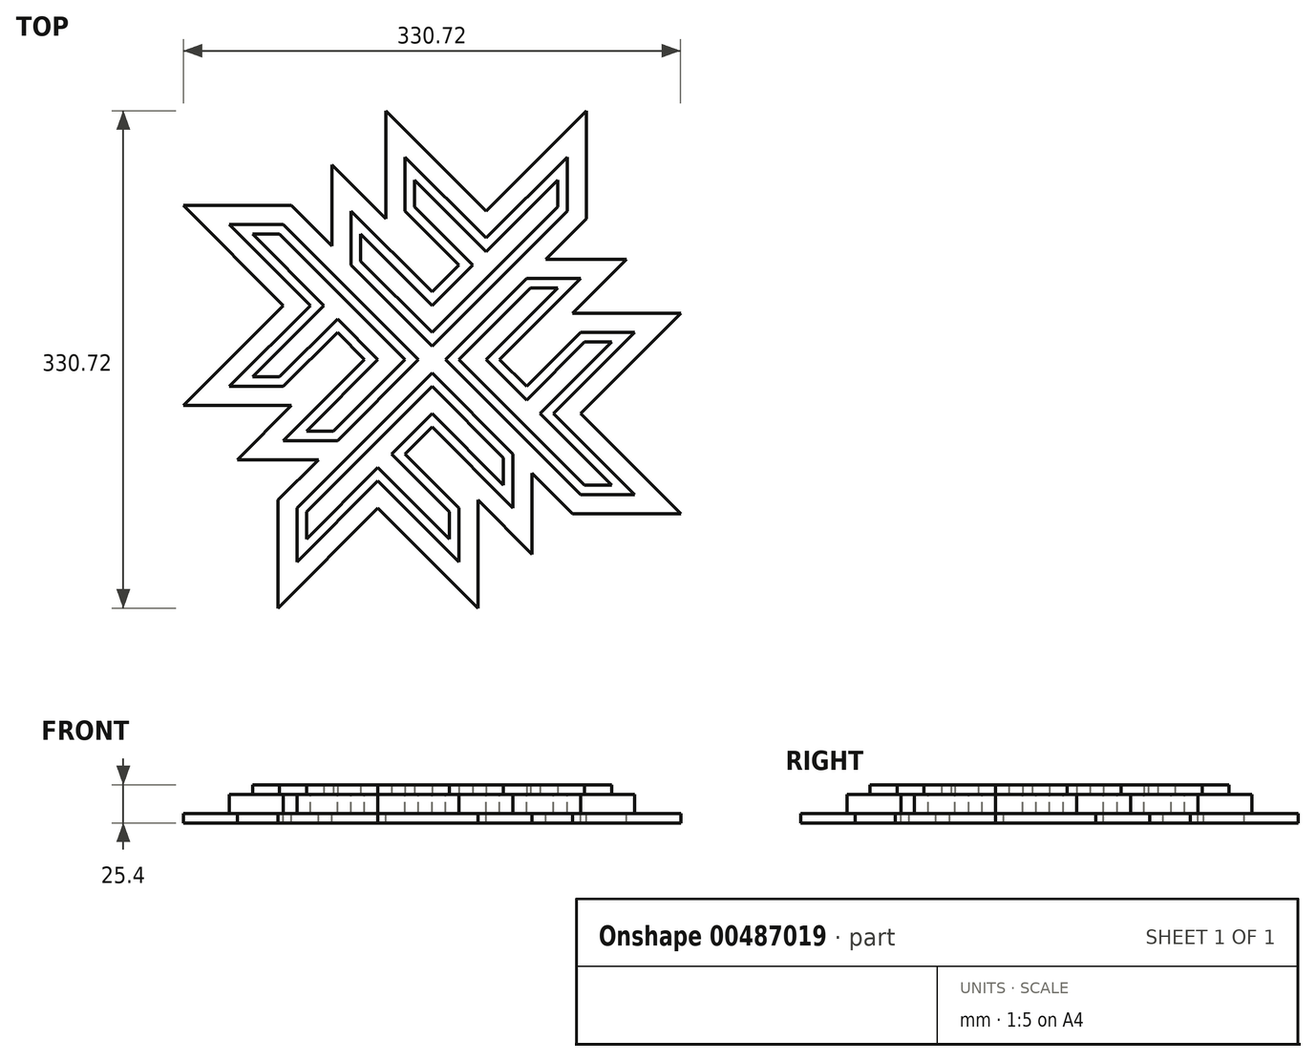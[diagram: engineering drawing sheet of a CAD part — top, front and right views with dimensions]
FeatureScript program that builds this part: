
annotation { "Feature Type Name" : "Feature", "Feature Type Description" : "" }
export const myFeature = defineFeature(function(context is Context, id is Id, definition is map)
    precondition{}
    {
        {
            var Q0;
            Q0=qCreatedBy(makeId("Top.planeOp"),FACE);
            var sketch = newSketch(context, id + "F0", { "sketchPlane" : qUnion([Q0])});
            skLineSegment(sketch, "E0", {"start": v(0, -30.17) * mm, "end": v(0, 96.83) * mm});
            skLineSegment(sketch, "E1", {"start": v(0, 96.83) * mm, "end": v(76.2, 96.83) * mm});
            skLineSegment(sketch, "E2", {"start": v(76.2, 96.83) * mm, "end": v(101.6, 71.43) * mm});
            skLineSegment(sketch, "E3", {"start": v(76.2, 96.83) * mm, "end": v(76.2, 71.43) * mm, "construction": true});
            skLineSegment(sketch, "E4", {"start": v(101.6, 71.43) * mm, "end": v(25.4, 71.43) * mm});
            skLineSegment(sketch, "E5", {"start": v(25.4, 71.43) * mm, "end": v(25.4, 46.03) * mm});
            skLineSegment(sketch, "E6", {"start": v(25.4, 46.03) * mm, "end": v(76.2, 46.03) * mm});
            skLineSegment(sketch, "E7", {"start": v(76.2, 46.03) * mm, "end": v(76.2, 20.63) * mm, "construction": true});
            skLineSegment(sketch, "E8", {"start": v(76.2, 46.03) * mm, "end": v(101.6, 20.63) * mm});
            skLineSegment(sketch, "E9", {"start": v(101.6, 20.63) * mm, "end": v(25.4, 20.63) * mm});
            skLineSegment(sketch, "E10", {"start": v(25.4, 20.63) * mm, "end": v(25.4, -55.57) * mm});
            skLineSegment(sketch, "E11", {"start": v(0, -30.17) * mm, "end": v(25.4, -55.57) * mm});
            skLineSegment(sketch, "E12.0", {"start": v(6.35, -27.54) * mm, "end": v(6.35, 90.48) * mm});
            skLineSegment(sketch, "E12.1", {"start": v(6.35, 90.48) * mm, "end": v(73.57, 90.48) * mm});
            skLineSegment(sketch, "E12.2", {"start": v(6.35, -27.54) * mm, "end": v(19.05, -40.24) * mm});
            skLineSegment(sketch, "E12.3", {"start": v(73.57, 90.48) * mm, "end": v(86.27, 77.78) * mm});
            skLineSegment(sketch, "E12.4", {"start": v(86.27, 77.78) * mm, "end": v(19.05, 77.78) * mm});
            skLineSegment(sketch, "E12.5", {"start": v(19.05, 77.78) * mm, "end": v(19.05, 39.68) * mm});
            skLineSegment(sketch, "E12.6", {"start": v(19.05, 26.98) * mm, "end": v(19.05, -40.24) * mm});
            skLineSegment(sketch, "E12.7", {"start": v(86.27, 26.98) * mm, "end": v(19.05, 26.98) * mm});
            skLineSegment(sketch, "E12.8", {"start": v(73.57, 39.68) * mm, "end": v(86.27, 26.98) * mm});
            skLineSegment(sketch, "E12.9", {"start": v(19.05, 39.68) * mm, "end": v(73.57, 39.68) * mm});
            skSolve(sketch);
        }
        {
            var Q0;
            Q0=makeQuery(id+"F0.imprint","IMPRINT",FACE,{"disambiguationData":[TD([[makeQuery(id+"F0.imprint","IMPRINT",EDGE,{"derivedFrom":sQuery(id+"F0.wireOp",EDGE,"E0")}),-1.0]])]});
            var Q1;
            Q1=makeQuery(id+"F0.imprint","IMPRINT",FACE,{"disambiguationData":[TD([[makeQuery(id+"F0.imprint","IMPRINT",EDGE,{"derivedFrom":sQuery(id+"F0.wireOp",EDGE,"E12.0")}),-1.0]])]});
            extrude(context, id + "F1", {"entities" : qUnion([Q0, Q1]), "oppositeDirection" : true, "depth" : 12.7 * mm});
        }
        {
            var Q0;
            Q0=makeQuery(id+"F1.opExtrude","CAP_FACE",FACE,{"disambiguationData":[OSD([sQuery(id+"F0.wireOp",EDGE,"E0"),sQuery(id+"F0.wireOp",EDGE,"E1"),sQuery(id+"F0.wireOp",EDGE,"E2"),sQuery(id+"F0.wireOp",EDGE,"E4"),sQuery(id+"F0.wireOp",EDGE,"E5"),sQuery(id+"F0.wireOp",EDGE,"E6"),sQuery(id+"F0.wireOp",EDGE,"E8"),sQuery(id+"F0.wireOp",EDGE,"E9"),sQuery(id+"F0.wireOp",EDGE,"E10"),sQuery(id+"F0.wireOp",EDGE,"E11")])],"isStart":true});
            var sketch = newSketch(context, id + "F2", { "sketchPlane" : qUnion([Q0])});
            skLineSegment(sketch, "E13", {"start": v(0, 96.83) * mm, "end": v(-6.35, 96.83) * mm, "construction": true});
            skLineSegment(sketch, "E14", {"start": v(-6.35, 96.83) * mm, "end": v(-6.35, 103.18) * mm, "construction": true});
            skPoint(sketch, "E15", {"position": v(-6.35, 103.18) * mm});
            skSolve(sketch);
        }
        {
            var Q0;
            Q0=qCreatedBy(makeId("Right.planeOp"),FACE);
            cPlane(context, id + "F3", {"entities" : qUnion([Q0]), "cplaneType" : CPlaneType.OFFSET, "offset" : 6.35 * mm, "oppositeDirection" : true, "width" : 152.4 * mm, "height" : 152.4 * mm});
        }
        {
            var Q0;
            Q0=qCreatedBy(id+"F3.planeOp",FACE);
            var sketch = newSketch(context, id + "F4", { "sketchPlane" : qUnion([Q0])});
            skPoint(sketch, "E16.0", {"position": v(103.18, 0) * mm});
            skLineSegment(sketch, "E17", {"start": v(103.18, 0) * mm, "end": v(103.18, -12.7) * mm, "construction": true});
            skSolve(sketch);
        }
        {
            var Q0;
            Q0=makeQuery(id+"F1.opExtrude","SWEPT_BODY",BODY,{"disambiguationData":[OSD([sQuery(id+"F0.wireOp",EDGE,"E0"),sQuery(id+"F0.wireOp",EDGE,"E1"),sQuery(id+"F0.wireOp",EDGE,"E2"),sQuery(id+"F0.wireOp",EDGE,"E4"),sQuery(id+"F0.wireOp",EDGE,"E5"),sQuery(id+"F0.wireOp",EDGE,"E6"),sQuery(id+"F0.wireOp",EDGE,"E8"),sQuery(id+"F0.wireOp",EDGE,"E9"),sQuery(id+"F0.wireOp",EDGE,"E10"),sQuery(id+"F0.wireOp",EDGE,"E11")])]});
            var Q1;
            Q1=sQuery(id+"F4.wireOp",EDGE,"E17");
            circularPattern(context, id + "F5", {"entities" : qUnion([Q0]), "axis" : qUnion([Q1]), "angle" : 360 * degree, "instanceCount" : 4, "equalSpace" : true});
        }
        {
            var Q0;
            Q0=makeQuery(id+"F5.opPattern","COPY",FACE,{"derivedFrom":makeQuery(id+"F1.opExtrude","CAP_FACE",FACE,{"disambiguationData":[OSD([sQuery(id+"F0.wireOp",EDGE,"E0"),sQuery(id+"F0.wireOp",EDGE,"E1"),sQuery(id+"F0.wireOp",EDGE,"E2"),sQuery(id+"F0.wireOp",EDGE,"E4"),sQuery(id+"F0.wireOp",EDGE,"E5"),sQuery(id+"F0.wireOp",EDGE,"E6"),sQuery(id+"F0.wireOp",EDGE,"E8"),sQuery(id+"F0.wireOp",EDGE,"E9"),sQuery(id+"F0.wireOp",EDGE,"E10"),sQuery(id+"F0.wireOp",EDGE,"E11")])],"isStart":false}),"instanceName":"1"});
            var sketch = newSketch(context, id + "F6", { "sketchPlane" : qUnion([Q0])});
            skLineSegment(sketch, "E18.0", {"start": v(0, -185.73) * mm, "end": v(25.4, -211.13) * mm});
            skLineSegment(sketch, "E18.1", {"start": v(-12.7, -236.53) * mm, "end": v(-12.7, -109.53) * mm});
            skLineSegment(sketch, "E18.2", {"start": v(-12.7, -236.53) * mm, "end": v(-38.1, -261.93) * mm});
            skLineSegment(sketch, "E18.3", {"start": v(-38.1, -185.73) * mm, "end": v(-38.1, -261.93) * mm});
            skLineSegment(sketch, "E18.4", {"start": v(-114.3, -185.73) * mm, "end": v(-38.1, -185.73) * mm});
            skLineSegment(sketch, "E18.5", {"start": v(-88.9, -160.33) * mm, "end": v(-114.3, -185.73) * mm});
            skLineSegment(sketch, "E18.6", {"start": v(-38.1, -160.33) * mm, "end": v(-88.9, -160.33) * mm});
            skLineSegment(sketch, "E18.7", {"start": v(-38.1, -134.93) * mm, "end": v(-38.1, -160.33) * mm});
            skLineSegment(sketch, "E18.8", {"start": v(-114.3, -134.93) * mm, "end": v(-38.1, -134.93) * mm});
            skLineSegment(sketch, "E18.9", {"start": v(-88.9, -109.53) * mm, "end": v(-114.3, -134.93) * mm});
            skLineSegment(sketch, "E18.10", {"start": v(-12.7, -109.53) * mm, "end": v(-88.9, -109.53) * mm});
            skLineSegment(sketch, "E18.11", {"start": v(-139.7, -96.83) * mm, "end": v(-12.7, -96.83) * mm});
            skLineSegment(sketch, "E18.12", {"start": v(-139.7, -96.83) * mm, "end": v(-165.1, -71.43) * mm});
            skLineSegment(sketch, "E18.13", {"start": v(-88.9, -71.43) * mm, "end": v(-165.1, -71.43) * mm});
            skLineSegment(sketch, "E18.14", {"start": v(-88.9, 4.77) * mm, "end": v(-88.9, -71.43) * mm});
            skLineSegment(sketch, "E18.15", {"start": v(-63.5, -20.63) * mm, "end": v(-88.9, 4.77) * mm});
            skLineSegment(sketch, "E18.16", {"start": v(-63.5, -71.43) * mm, "end": v(-63.5, -20.63) * mm});
            skLineSegment(sketch, "E18.17", {"start": v(-38.1, -71.43) * mm, "end": v(-63.5, -71.43) * mm});
            skLineSegment(sketch, "E18.18", {"start": v(-38.1, 4.77) * mm, "end": v(-38.1, -71.43) * mm});
            skLineSegment(sketch, "E18.19", {"start": v(-12.7, -20.63) * mm, "end": v(-38.1, 4.77) * mm});
            skLineSegment(sketch, "E18.20", {"start": v(-12.7, -96.83) * mm, "end": v(-12.7, -20.63) * mm});
            skLineSegment(sketch, "E18.21", {"start": v(0, 30.17) * mm, "end": v(0, -96.83) * mm});
            skLineSegment(sketch, "E18.22", {"start": v(0, -96.83) * mm, "end": v(76.2, -96.83) * mm});
            skLineSegment(sketch, "E18.23", {"start": v(76.2, -96.83) * mm, "end": v(101.6, -71.43) * mm});
            skLineSegment(sketch, "E18.24", {"start": v(101.6, -71.43) * mm, "end": v(25.4, -71.43) * mm});
            skLineSegment(sketch, "E18.25", {"start": v(25.4, -71.43) * mm, "end": v(25.4, -46.03) * mm});
            skLineSegment(sketch, "E18.26", {"start": v(25.4, -46.03) * mm, "end": v(76.2, -46.03) * mm});
            skLineSegment(sketch, "E18.27", {"start": v(76.2, -46.03) * mm, "end": v(101.6, -20.63) * mm});
            skLineSegment(sketch, "E18.28", {"start": v(101.6, -20.63) * mm, "end": v(25.4, -20.63) * mm});
            skLineSegment(sketch, "E18.29", {"start": v(25.4, -20.63) * mm, "end": v(25.4, 55.57) * mm});
            skLineSegment(sketch, "E18.30", {"start": v(0, 30.17) * mm, "end": v(25.4, 55.57) * mm});
            skLineSegment(sketch, "E18.31", {"start": v(127, -109.53) * mm, "end": v(0, -109.53) * mm});
            skLineSegment(sketch, "E18.32", {"start": v(0, -109.53) * mm, "end": v(0, -185.73) * mm});
            skLineSegment(sketch, "E18.33", {"start": v(25.4, -211.13) * mm, "end": v(25.4, -134.93) * mm});
            skLineSegment(sketch, "E18.34", {"start": v(25.4, -134.93) * mm, "end": v(50.8, -134.93) * mm});
            skLineSegment(sketch, "E18.35", {"start": v(50.8, -134.93) * mm, "end": v(50.8, -185.73) * mm});
            skLineSegment(sketch, "E18.36", {"start": v(50.8, -185.73) * mm, "end": v(76.2, -211.13) * mm});
            skLineSegment(sketch, "E18.37", {"start": v(76.2, -211.13) * mm, "end": v(76.2, -134.93) * mm});
            skLineSegment(sketch, "E18.38", {"start": v(76.2, -134.93) * mm, "end": v(152.4, -134.93) * mm});
            skLineSegment(sketch, "E18.39", {"start": v(127, -109.53) * mm, "end": v(152.4, -134.93) * mm});
            skLineSegment(sketch, "E19.0", {"start": v(0, -241.79) * mm, "end": v(-50.8, -292.59) * mm});
            skLineSegment(sketch, "E19.1", {"start": v(-50.8, -198.43) * mm, "end": v(-50.8, -292.59) * mm});
            skLineSegment(sketch, "E19.3", {"start": v(-144.96, -198.43) * mm, "end": v(-50.8, -198.43) * mm});
            skLineSegment(sketch, "E19.4", {"start": v(-94.16, -147.63) * mm, "end": v(-144.96, -198.43) * mm});
            skLineSegment(sketch, "E20", {"start": v(-144.96, -147.63) * mm, "end": v(-94.16, -147.63) * mm});
            skPoint(sketch, "E21.0", {"position": v(-6.35, -103.18) * mm});
            skLineSegment(sketch, "E22.1.1", {"start": v(132.26, -96.83) * mm, "end": v(183.06, -147.63) * mm});
            skLineSegment(sketch, "E22.1.2", {"start": v(88.9, -147.63) * mm, "end": v(183.06, -147.63) * mm});
            skLineSegment(sketch, "E22.1.3", {"start": v(88.9, -241.79) * mm, "end": v(88.9, -147.63) * mm});
            skLineSegment(sketch, "E22.1.4", {"start": v(38.1, -190.99) * mm, "end": v(88.9, -241.79) * mm});
            skLineSegment(sketch, "E22.1.5", {"start": v(38.1, -241.79) * mm, "end": v(38.1, -190.99) * mm});
            skLineSegment(sketch, "E22.2.1", {"start": v(-12.7, 35.43) * mm, "end": v(38.1, 86.23) * mm});
            skLineSegment(sketch, "E22.2.2", {"start": v(38.1, -7.93) * mm, "end": v(38.1, 86.23) * mm});
            skLineSegment(sketch, "E22.2.3", {"start": v(132.26, -7.93) * mm, "end": v(38.1, -7.93) * mm});
            skLineSegment(sketch, "E22.2.4", {"start": v(81.46, -58.73) * mm, "end": v(132.26, -7.93) * mm});
            skLineSegment(sketch, "E22.2.5", {"start": v(132.26, -58.73) * mm, "end": v(81.46, -58.73) * mm});
            skLineSegment(sketch, "E22.3.1", {"start": v(-144.96, -109.53) * mm, "end": v(-195.76, -58.73) * mm});
            skLineSegment(sketch, "E22.3.2", {"start": v(-101.6, -58.73) * mm, "end": v(-195.76, -58.73) * mm});
            skLineSegment(sketch, "E22.3.3", {"start": v(-101.6, 35.43) * mm, "end": v(-101.6, -58.73) * mm});
            skLineSegment(sketch, "E22.3.4", {"start": v(-50.8, -15.37) * mm, "end": v(-101.6, 35.43) * mm});
            skLineSegment(sketch, "E22.3.5", {"start": v(-50.8, 35.43) * mm, "end": v(-50.8, -15.37) * mm});
            skLineSegment(sketch, "E23", {"start": v(0, -241.79) * mm, "end": v(0, -203.69) * mm});
            skLineSegment(sketch, "E24", {"start": v(38.1, -241.79) * mm, "end": v(0, -203.69) * mm});
            skLineSegment(sketch, "E25", {"start": v(132.26, -96.83) * mm, "end": v(94.16, -96.83) * mm});
            skLineSegment(sketch, "E26", {"start": v(132.26, -58.73) * mm, "end": v(94.16, -96.83) * mm});
            skLineSegment(sketch, "E27", {"start": v(-12.7, 35.43) * mm, "end": v(-12.7, -2.67) * mm});
            skLineSegment(sketch, "E28", {"start": v(-12.7, -2.67) * mm, "end": v(-50.8, 35.43) * mm});
            skLineSegment(sketch, "E29", {"start": v(-144.96, -109.53) * mm, "end": v(-106.86, -109.53) * mm});
            skLineSegment(sketch, "E30", {"start": v(-144.96, -147.63) * mm, "end": v(-106.86, -109.53) * mm});
            skSolve(sketch);
        }
        {
            var Q0;
            Q0=makeQuery(id+"F6.imprint","IMPRINT",FACE,{"disambiguationData":[TD([[makeQuery(id+"F6.imprint","IMPRINT",EDGE,{"derivedFrom":sQuery(id+"F6.wireOp",EDGE,"E18.0")}),-1.0]])]});
            var Q1;
            Q1=makeQuery(id+"F6.imprint","IMPRINT",FACE,{"disambiguationData":[TD([[makeQuery(id+"F6.imprint","IMPRINT",EDGE,{"derivedFrom":sQuery(id+"F6.wireOp",EDGE,"E18.11")}),1.0]])]});
            var Q2;
            Q2=makeQuery(id+"F6.imprint","IMPRINT",FACE,{"disambiguationData":[TD([[makeQuery(id+"F6.imprint","IMPRINT",EDGE,{"derivedFrom":sQuery(id+"F6.wireOp",EDGE,"E18.21")}),1.0]])]});
            var Q3;
            Q3=makeQuery(id+"F6.imprint","IMPRINT",FACE,{"disambiguationData":[TD([[makeQuery(id+"F6.imprint","IMPRINT",EDGE,{"derivedFrom":sQuery(id+"F6.wireOp",EDGE,"E18.0")}),1.0]])]});
            var Q4;
            Q4=makeQuery(id+"F6.imprint","IMPRINT",FACE,{"disambiguationData":[TD([[makeQuery(id+"F6.imprint","IMPRINT",EDGE,{"derivedFrom":sQuery(id+"F6.wireOp",EDGE,"E18.1")}),1.0]])]});
            extrude(context, id + "F7", {"entities" : qUnion([Q0, Q1, Q2, Q3, Q4]), "depth" : 6.35 * mm});
        }
        {
            var Q0;
            Q0=makeQuery(id+"F7.opExtrude","SWEPT_BODY",BODY,{"disambiguationData":[OSD([sQuery(id+"F6.wireOp",EDGE,"E19.0"),sQuery(id+"F6.wireOp",EDGE,"E19.1"),sQuery(id+"F6.wireOp",EDGE,"E19.3"),sQuery(id+"F6.wireOp",EDGE,"E19.4"),sQuery(id+"F6.wireOp",EDGE,"E20"),sQuery(id+"F6.wireOp",EDGE,"E22.1.1"),sQuery(id+"F6.wireOp",EDGE,"E22.1.2"),sQuery(id+"F6.wireOp",EDGE,"E22.1.3"),sQuery(id+"F6.wireOp",EDGE,"E22.1.4"),sQuery(id+"F6.wireOp",EDGE,"E22.1.5"),sQuery(id+"F6.wireOp",EDGE,"E22.2.1"),sQuery(id+"F6.wireOp",EDGE,"E22.2.2"),sQuery(id+"F6.wireOp",EDGE,"E22.2.3"),sQuery(id+"F6.wireOp",EDGE,"E22.2.4"),sQuery(id+"F6.wireOp",EDGE,"E22.2.5"),sQuery(id+"F6.wireOp",EDGE,"E22.3.1"),sQuery(id+"F6.wireOp",EDGE,"E22.3.2"),sQuery(id+"F6.wireOp",EDGE,"E22.3.3"),sQuery(id+"F6.wireOp",EDGE,"E22.3.4"),sQuery(id+"F6.wireOp",EDGE,"E22.3.5"),sQuery(id+"F6.wireOp",EDGE,"E23"),sQuery(id+"F6.wireOp",EDGE,"E24"),sQuery(id+"F6.wireOp",EDGE,"E25"),sQuery(id+"F6.wireOp",EDGE,"E26"),sQuery(id+"F6.wireOp",EDGE,"E27"),sQuery(id+"F6.wireOp",EDGE,"E28"),sQuery(id+"F6.wireOp",EDGE,"E29"),sQuery(id+"F6.wireOp",EDGE,"E30")])]});
            var Q1;
            Q1=makeQuery(id+"F1.opExtrude","SWEPT_BODY",BODY,{"disambiguationData":[OSD([sQuery(id+"F0.wireOp",EDGE,"E0"),sQuery(id+"F0.wireOp",EDGE,"E1"),sQuery(id+"F0.wireOp",EDGE,"E2"),sQuery(id+"F0.wireOp",EDGE,"E4"),sQuery(id+"F0.wireOp",EDGE,"E5"),sQuery(id+"F0.wireOp",EDGE,"E6"),sQuery(id+"F0.wireOp",EDGE,"E8"),sQuery(id+"F0.wireOp",EDGE,"E9"),sQuery(id+"F0.wireOp",EDGE,"E10"),sQuery(id+"F0.wireOp",EDGE,"E11")])]});
            var Q2;
            Q2=makeQuery(id+"F5.opPattern","COPY",BODY,{"derivedFrom":makeQuery(id+"F1.opExtrude","SWEPT_BODY",BODY,{"disambiguationData":[OSD([sQuery(id+"F0.wireOp",EDGE,"E0"),sQuery(id+"F0.wireOp",EDGE,"E1"),sQuery(id+"F0.wireOp",EDGE,"E2"),sQuery(id+"F0.wireOp",EDGE,"E4"),sQuery(id+"F0.wireOp",EDGE,"E5"),sQuery(id+"F0.wireOp",EDGE,"E6"),sQuery(id+"F0.wireOp",EDGE,"E8"),sQuery(id+"F0.wireOp",EDGE,"E9"),sQuery(id+"F0.wireOp",EDGE,"E10"),sQuery(id+"F0.wireOp",EDGE,"E11")])]}),"instanceName":"1"});
            var Q3;
            Q3=makeQuery(id+"F5.opPattern","COPY",BODY,{"derivedFrom":makeQuery(id+"F1.opExtrude","SWEPT_BODY",BODY,{"disambiguationData":[OSD([sQuery(id+"F0.wireOp",EDGE,"E0"),sQuery(id+"F0.wireOp",EDGE,"E1"),sQuery(id+"F0.wireOp",EDGE,"E2"),sQuery(id+"F0.wireOp",EDGE,"E4"),sQuery(id+"F0.wireOp",EDGE,"E5"),sQuery(id+"F0.wireOp",EDGE,"E6"),sQuery(id+"F0.wireOp",EDGE,"E8"),sQuery(id+"F0.wireOp",EDGE,"E9"),sQuery(id+"F0.wireOp",EDGE,"E10"),sQuery(id+"F0.wireOp",EDGE,"E11")])]}),"instanceName":"2"});
            var Q4;
            Q4=makeQuery(id+"F5.opPattern","COPY",BODY,{"derivedFrom":makeQuery(id+"F1.opExtrude","SWEPT_BODY",BODY,{"disambiguationData":[OSD([sQuery(id+"F0.wireOp",EDGE,"E0"),sQuery(id+"F0.wireOp",EDGE,"E1"),sQuery(id+"F0.wireOp",EDGE,"E2"),sQuery(id+"F0.wireOp",EDGE,"E4"),sQuery(id+"F0.wireOp",EDGE,"E5"),sQuery(id+"F0.wireOp",EDGE,"E6"),sQuery(id+"F0.wireOp",EDGE,"E8"),sQuery(id+"F0.wireOp",EDGE,"E9"),sQuery(id+"F0.wireOp",EDGE,"E10"),sQuery(id+"F0.wireOp",EDGE,"E11")])]}),"instanceName":"3"});
            var Q5;
            Q5=sQuery(id+"F2.wireOp",VERTEX,"E15");
            var Q6;
            Q6=qCreatedBy(makeId("Origin.pointOp"),VERTEX);
            transform(context, id + "F8", {"entities" : qUnion([Q0, Q1, Q2, Q3, Q4]), "transformType" : TransformType.TRANSLATION_ENTITY, "oppositeDirectionEntity" : false, "transformLine" : qUnion([Q5, Q6]), "makeCopy" : false});
        }
        {
            var Q0;
            Q0=makeQuery(id+"F1.opExtrude","CAP_FACE",FACE,{"disambiguationData":[OSD([sQuery(id+"F0.wireOp",EDGE,"E0"),sQuery(id+"F0.wireOp",EDGE,"E1"),sQuery(id+"F0.wireOp",EDGE,"E2"),sQuery(id+"F0.wireOp",EDGE,"E4"),sQuery(id+"F0.wireOp",EDGE,"E5"),sQuery(id+"F0.wireOp",EDGE,"E6"),sQuery(id+"F0.wireOp",EDGE,"E8"),sQuery(id+"F0.wireOp",EDGE,"E9"),sQuery(id+"F0.wireOp",EDGE,"E10"),sQuery(id+"F0.wireOp",EDGE,"E11")])],"isStart":true});
            var sketch = newSketch(context, id + "F9", { "sketchPlane" : qUnion([Q0])});
            skLineSegment(sketch, "E31.0.0", {"start": v(-6.35, -6.35) * mm, "end": v(-133.35, -6.35) * mm});
            skLineSegment(sketch, "E31.0.1", {"start": v(-133.35, -6.35) * mm, "end": v(-158.75, -31.75) * mm});
            skLineSegment(sketch, "E31.0.2", {"start": v(-158.75, -31.75) * mm, "end": v(-82.55, -31.75) * mm});
            skLineSegment(sketch, "E31.0.3", {"start": v(-82.55, -31.75) * mm, "end": v(-82.55, -107.95) * mm});
            skLineSegment(sketch, "E31.0.4", {"start": v(-82.55, -107.95) * mm, "end": v(-57.15, -82.55) * mm});
            skLineSegment(sketch, "E31.0.5", {"start": v(-57.15, -82.55) * mm, "end": v(-57.15, -31.75) * mm});
            skLineSegment(sketch, "E31.0.6", {"start": v(-57.15, -31.75) * mm, "end": v(-31.75, -31.75) * mm});
            skLineSegment(sketch, "E31.0.7", {"start": v(-31.75, -31.75) * mm, "end": v(-31.75, -107.95) * mm});
            skLineSegment(sketch, "E31.0.8", {"start": v(-31.75, -107.95) * mm, "end": v(-6.35, -82.55) * mm});
            skLineSegment(sketch, "E31.0.9", {"start": v(-6.35, -82.55) * mm, "end": v(-6.35, -6.35) * mm});
            skLineSegment(sketch, "E31.2.0", {"start": v(6.35, 6.35) * mm, "end": v(133.35, 6.35) * mm});
            skLineSegment(sketch, "E31.2.1", {"start": v(133.35, 6.35) * mm, "end": v(158.75, 31.75) * mm});
            skLineSegment(sketch, "E31.2.2", {"start": v(158.75, 31.75) * mm, "end": v(82.55, 31.75) * mm});
            skLineSegment(sketch, "E31.2.3", {"start": v(82.55, 31.75) * mm, "end": v(82.55, 107.95) * mm});
            skLineSegment(sketch, "E31.2.4", {"start": v(82.55, 107.95) * mm, "end": v(57.15, 82.55) * mm});
            skLineSegment(sketch, "E31.2.5", {"start": v(57.15, 82.55) * mm, "end": v(57.15, 31.75) * mm});
            skLineSegment(sketch, "E31.2.6", {"start": v(57.15, 31.75) * mm, "end": v(31.75, 31.75) * mm});
            skLineSegment(sketch, "E31.2.7", {"start": v(31.75, 31.75) * mm, "end": v(31.75, 107.95) * mm});
            skLineSegment(sketch, "E31.2.8", {"start": v(31.75, 107.95) * mm, "end": v(6.35, 82.55) * mm});
            skLineSegment(sketch, "E31.2.9", {"start": v(6.35, 82.55) * mm, "end": v(6.35, 6.35) * mm});
            skLineSegment(sketch, "E31.3.0", {"start": v(-6.35, 6.35) * mm, "end": v(-6.35, 133.35) * mm});
            skLineSegment(sketch, "E31.3.1", {"start": v(-6.35, 133.35) * mm, "end": v(-31.75, 158.75) * mm});
            skLineSegment(sketch, "E31.3.2", {"start": v(-31.75, 158.75) * mm, "end": v(-31.75, 82.55) * mm});
            skLineSegment(sketch, "E31.3.3", {"start": v(-31.75, 82.55) * mm, "end": v(-107.95, 82.55) * mm});
            skLineSegment(sketch, "E31.3.4", {"start": v(-107.95, 82.55) * mm, "end": v(-82.55, 57.15) * mm});
            skLineSegment(sketch, "E31.3.5", {"start": v(-82.55, 57.15) * mm, "end": v(-31.75, 57.15) * mm});
            skLineSegment(sketch, "E31.3.6", {"start": v(-31.75, 57.15) * mm, "end": v(-31.75, 31.75) * mm});
            skLineSegment(sketch, "E31.3.7", {"start": v(-31.75, 31.75) * mm, "end": v(-107.95, 31.75) * mm});
            skLineSegment(sketch, "E31.3.8", {"start": v(-107.95, 31.75) * mm, "end": v(-82.55, 6.35) * mm});
            skLineSegment(sketch, "E31.3.9", {"start": v(-82.55, 6.35) * mm, "end": v(-6.35, 6.35) * mm});
            skLineSegment(sketch, "E32.0", {"start": v(6.35, -133.35) * mm, "end": v(6.35, -6.35) * mm});
            skLineSegment(sketch, "E32.1", {"start": v(6.35, -6.35) * mm, "end": v(82.55, -6.35) * mm});
            skLineSegment(sketch, "E32.2", {"start": v(82.55, -6.35) * mm, "end": v(107.95, -31.75) * mm});
            skLineSegment(sketch, "E32.3", {"start": v(107.95, -31.75) * mm, "end": v(31.75, -31.75) * mm});
            skLineSegment(sketch, "E32.4", {"start": v(31.75, -31.75) * mm, "end": v(31.75, -57.15) * mm});
            skLineSegment(sketch, "E32.5", {"start": v(31.75, -57.15) * mm, "end": v(82.55, -57.15) * mm});
            skLineSegment(sketch, "E32.6", {"start": v(82.55, -57.15) * mm, "end": v(107.95, -82.55) * mm});
            skLineSegment(sketch, "E32.7", {"start": v(107.95, -82.55) * mm, "end": v(31.75, -82.55) * mm});
            skLineSegment(sketch, "E32.8", {"start": v(31.75, -82.55) * mm, "end": v(31.75, -158.75) * mm});
            skLineSegment(sketch, "E32.9", {"start": v(6.35, -133.35) * mm, "end": v(31.75, -158.75) * mm});
            skLineSegment(sketch, "E33.0", {"start": v(12.7, -130.72) * mm, "end": v(12.7, -12.7) * mm});
            skLineSegment(sketch, "E33.1", {"start": v(12.7, -130.72) * mm, "end": v(25.4, -143.42) * mm});
            skLineSegment(sketch, "E33.2", {"start": v(12.7, -12.7) * mm, "end": v(79.92, -12.7) * mm});
            skLineSegment(sketch, "E33.3", {"start": v(25.4, -76.2) * mm, "end": v(25.4, -143.42) * mm});
            skLineSegment(sketch, "E33.4", {"start": v(92.62, -76.2) * mm, "end": v(25.4, -76.2) * mm});
            skLineSegment(sketch, "E33.5", {"start": v(79.92, -63.5) * mm, "end": v(92.62, -76.2) * mm});
            skLineSegment(sketch, "E33.6", {"start": v(79.92, -12.7) * mm, "end": v(92.62, -25.4) * mm});
            skLineSegment(sketch, "E33.7", {"start": v(92.62, -25.4) * mm, "end": v(25.4, -25.4) * mm});
            skLineSegment(sketch, "E33.8", {"start": v(25.4, -25.4) * mm, "end": v(25.4, -63.5) * mm});
            skLineSegment(sketch, "E33.9", {"start": v(25.4, -63.5) * mm, "end": v(79.92, -63.5) * mm});
            skLineSegment(sketch, "E34.0", {"start": v(-25.4, -92.62) * mm, "end": v(-12.7, -79.92) * mm});
            skLineSegment(sketch, "E34.1", {"start": v(-25.4, -25.4) * mm, "end": v(-25.4, -92.62) * mm});
            skLineSegment(sketch, "E34.2", {"start": v(-12.7, -79.92) * mm, "end": v(-12.7, -12.7) * mm});
            skLineSegment(sketch, "E34.3", {"start": v(-63.5, -25.4) * mm, "end": v(-25.4, -25.4) * mm});
            skLineSegment(sketch, "E34.4", {"start": v(-63.5, -79.92) * mm, "end": v(-63.5, -25.4) * mm});
            skLineSegment(sketch, "E34.5", {"start": v(-76.2, -92.62) * mm, "end": v(-63.5, -79.92) * mm});
            skLineSegment(sketch, "E34.6", {"start": v(-12.7, -12.7) * mm, "end": v(-130.72, -12.7) * mm});
            skLineSegment(sketch, "E34.7", {"start": v(-130.72, -12.7) * mm, "end": v(-143.42, -25.4) * mm});
            skLineSegment(sketch, "E34.8", {"start": v(-143.42, -25.4) * mm, "end": v(-76.2, -25.4) * mm});
            skLineSegment(sketch, "E34.9", {"start": v(-76.2, -25.4) * mm, "end": v(-76.2, -92.62) * mm});
            skLineSegment(sketch, "E35.0", {"start": v(-12.7, 130.72) * mm, "end": v(-25.4, 143.42) * mm});
            skLineSegment(sketch, "E35.1", {"start": v(-12.7, 12.7) * mm, "end": v(-12.7, 130.72) * mm});
            skLineSegment(sketch, "E35.2", {"start": v(-25.4, 143.42) * mm, "end": v(-25.4, 76.2) * mm});
            skLineSegment(sketch, "E35.3", {"start": v(-79.92, 12.7) * mm, "end": v(-12.7, 12.7) * mm});
            skLineSegment(sketch, "E35.4", {"start": v(-92.62, 25.4) * mm, "end": v(-79.92, 12.7) * mm});
            skLineSegment(sketch, "E35.5", {"start": v(-25.4, 25.4) * mm, "end": v(-92.62, 25.4) * mm});
            skLineSegment(sketch, "E35.6", {"start": v(-25.4, 76.2) * mm, "end": v(-92.62, 76.2) * mm});
            skLineSegment(sketch, "E35.7", {"start": v(-92.62, 76.2) * mm, "end": v(-79.92, 63.5) * mm});
            skLineSegment(sketch, "E35.8", {"start": v(-79.92, 63.5) * mm, "end": v(-25.4, 63.5) * mm});
            skLineSegment(sketch, "E35.9", {"start": v(-25.4, 63.5) * mm, "end": v(-25.4, 25.4) * mm});
            skLineSegment(sketch, "E36.0", {"start": v(63.5, 25.4) * mm, "end": v(25.4, 25.4) * mm});
            skLineSegment(sketch, "E36.1", {"start": v(63.5, 79.92) * mm, "end": v(63.5, 25.4) * mm});
            skLineSegment(sketch, "E36.2", {"start": v(25.4, 25.4) * mm, "end": v(25.4, 92.62) * mm});
            skLineSegment(sketch, "E36.3", {"start": v(76.2, 92.62) * mm, "end": v(63.5, 79.92) * mm});
            skLineSegment(sketch, "E36.4", {"start": v(76.2, 25.4) * mm, "end": v(76.2, 92.62) * mm});
            skLineSegment(sketch, "E36.5", {"start": v(143.42, 25.4) * mm, "end": v(76.2, 25.4) * mm});
            skLineSegment(sketch, "E36.6", {"start": v(25.4, 92.62) * mm, "end": v(12.7, 79.92) * mm});
            skLineSegment(sketch, "E36.7", {"start": v(12.7, 79.92) * mm, "end": v(12.7, 12.7) * mm});
            skLineSegment(sketch, "E36.8", {"start": v(12.7, 12.7) * mm, "end": v(130.72, 12.7) * mm});
            skLineSegment(sketch, "E36.9", {"start": v(130.72, 12.7) * mm, "end": v(143.42, 25.4) * mm});
            skSolve(sketch);
        }
        {
            var Q0;
            Q0=makeQuery(id+"F9.imprint","IMPRINT",FACE,{"disambiguationData":[TD([[makeQuery(id+"F9.imprint","IMPRINT",EDGE,{"derivedFrom":sQuery(id+"F9.wireOp",EDGE,"E35.0")}),1.0]])]});
            var Q1;
            Q1=makeQuery(id+"F9.imprint","IMPRINT",FACE,{"disambiguationData":[TD([[makeQuery(id+"F9.imprint","IMPRINT",EDGE,{"derivedFrom":sQuery(id+"F9.wireOp",EDGE,"E36.0")}),1.0]])]});
            var Q2;
            Q2=makeQuery(id+"F9.imprint","IMPRINT",FACE,{"disambiguationData":[TD([[makeQuery(id+"F9.imprint","IMPRINT",EDGE,{"derivedFrom":sQuery(id+"F9.wireOp",EDGE,"E33.0")}),-1.0]])]});
            var Q3;
            Q3=makeQuery(id+"F9.imprint","IMPRINT",FACE,{"disambiguationData":[TD([[makeQuery(id+"F9.imprint","IMPRINT",EDGE,{"derivedFrom":sQuery(id+"F9.wireOp",EDGE,"E34.0")}),1.0]])]});
            extrude(context, id + "F10", {"entities" : qUnion([Q0, Q1, Q2, Q3]), "depth" : 6.35 * mm});
        }
        {
            var Q0;
            Q0=qCreatedBy(makeId("Front.planeOp"),FACE);
            var sketch = newSketch(context, id + "F11", { "sketchPlane" : qUnion([Q0])});
            skLineSegment(sketch, "E37", {"start": v(0, 0) * mm, "end": v(0, -12.7) * mm, "construction": true});
            skSolve(sketch);
        }
        {
            var Q0;
            Q0=makeQuery(id+"F1.opExtrude","SWEPT_BODY",BODY,{"disambiguationData":[OSD([sQuery(id+"F0.wireOp",EDGE,"E0"),sQuery(id+"F0.wireOp",EDGE,"E1"),sQuery(id+"F0.wireOp",EDGE,"E2"),sQuery(id+"F0.wireOp",EDGE,"E4"),sQuery(id+"F0.wireOp",EDGE,"E5"),sQuery(id+"F0.wireOp",EDGE,"E6"),sQuery(id+"F0.wireOp",EDGE,"E8"),sQuery(id+"F0.wireOp",EDGE,"E9"),sQuery(id+"F0.wireOp",EDGE,"E10"),sQuery(id+"F0.wireOp",EDGE,"E11")])]});
            var Q1;
            Q1=makeQuery(id+"F5.opPattern","COPY",BODY,{"derivedFrom":makeQuery(id+"F1.opExtrude","SWEPT_BODY",BODY,{"disambiguationData":[OSD([sQuery(id+"F0.wireOp",EDGE,"E0"),sQuery(id+"F0.wireOp",EDGE,"E1"),sQuery(id+"F0.wireOp",EDGE,"E2"),sQuery(id+"F0.wireOp",EDGE,"E4"),sQuery(id+"F0.wireOp",EDGE,"E5"),sQuery(id+"F0.wireOp",EDGE,"E6"),sQuery(id+"F0.wireOp",EDGE,"E8"),sQuery(id+"F0.wireOp",EDGE,"E9"),sQuery(id+"F0.wireOp",EDGE,"E10"),sQuery(id+"F0.wireOp",EDGE,"E11")])]}),"instanceName":"2"});
            var Q2;
            Q2=makeQuery(id+"F5.opPattern","COPY",BODY,{"derivedFrom":makeQuery(id+"F1.opExtrude","SWEPT_BODY",BODY,{"disambiguationData":[OSD([sQuery(id+"F0.wireOp",EDGE,"E0"),sQuery(id+"F0.wireOp",EDGE,"E1"),sQuery(id+"F0.wireOp",EDGE,"E2"),sQuery(id+"F0.wireOp",EDGE,"E4"),sQuery(id+"F0.wireOp",EDGE,"E5"),sQuery(id+"F0.wireOp",EDGE,"E6"),sQuery(id+"F0.wireOp",EDGE,"E8"),sQuery(id+"F0.wireOp",EDGE,"E9"),sQuery(id+"F0.wireOp",EDGE,"E10"),sQuery(id+"F0.wireOp",EDGE,"E11")])]}),"instanceName":"3"});
            var Q3;
            Q3=makeQuery(id+"F5.opPattern","COPY",BODY,{"derivedFrom":makeQuery(id+"F1.opExtrude","SWEPT_BODY",BODY,{"disambiguationData":[OSD([sQuery(id+"F0.wireOp",EDGE,"E0"),sQuery(id+"F0.wireOp",EDGE,"E1"),sQuery(id+"F0.wireOp",EDGE,"E2"),sQuery(id+"F0.wireOp",EDGE,"E4"),sQuery(id+"F0.wireOp",EDGE,"E5"),sQuery(id+"F0.wireOp",EDGE,"E6"),sQuery(id+"F0.wireOp",EDGE,"E8"),sQuery(id+"F0.wireOp",EDGE,"E9"),sQuery(id+"F0.wireOp",EDGE,"E10"),sQuery(id+"F0.wireOp",EDGE,"E11")])]}),"instanceName":"1"});
            var Q4;
            Q4=makeQuery(id+"F7.opExtrude","SWEPT_BODY",BODY,{"disambiguationData":[OSD([sQuery(id+"F6.wireOp",EDGE,"E19.0"),sQuery(id+"F6.wireOp",EDGE,"E19.1"),sQuery(id+"F6.wireOp",EDGE,"E19.3"),sQuery(id+"F6.wireOp",EDGE,"E19.4"),sQuery(id+"F6.wireOp",EDGE,"E20"),sQuery(id+"F6.wireOp",EDGE,"E22.1.1"),sQuery(id+"F6.wireOp",EDGE,"E22.1.2"),sQuery(id+"F6.wireOp",EDGE,"E22.1.3"),sQuery(id+"F6.wireOp",EDGE,"E22.1.4"),sQuery(id+"F6.wireOp",EDGE,"E22.1.5"),sQuery(id+"F6.wireOp",EDGE,"E22.2.1"),sQuery(id+"F6.wireOp",EDGE,"E22.2.2"),sQuery(id+"F6.wireOp",EDGE,"E22.2.3"),sQuery(id+"F6.wireOp",EDGE,"E22.2.4"),sQuery(id+"F6.wireOp",EDGE,"E22.2.5"),sQuery(id+"F6.wireOp",EDGE,"E22.3.1"),sQuery(id+"F6.wireOp",EDGE,"E22.3.2"),sQuery(id+"F6.wireOp",EDGE,"E22.3.3"),sQuery(id+"F6.wireOp",EDGE,"E22.3.4"),sQuery(id+"F6.wireOp",EDGE,"E22.3.5"),sQuery(id+"F6.wireOp",EDGE,"E23"),sQuery(id+"F6.wireOp",EDGE,"E24"),sQuery(id+"F6.wireOp",EDGE,"E25"),sQuery(id+"F6.wireOp",EDGE,"E26"),sQuery(id+"F6.wireOp",EDGE,"E27"),sQuery(id+"F6.wireOp",EDGE,"E28"),sQuery(id+"F6.wireOp",EDGE,"E29"),sQuery(id+"F6.wireOp",EDGE,"E30")])]});
            var Q5;
            Q5=makeQuery(id+"F10.opExtrude","SWEPT_BODY",BODY,{"disambiguationData":[OSD([sQuery(id+"F9.wireOp",EDGE,"E36.0"),sQuery(id+"F9.wireOp",EDGE,"E36.1"),sQuery(id+"F9.wireOp",EDGE,"E36.2"),sQuery(id+"F9.wireOp",EDGE,"E36.3"),sQuery(id+"F9.wireOp",EDGE,"E36.4"),sQuery(id+"F9.wireOp",EDGE,"E36.5"),sQuery(id+"F9.wireOp",EDGE,"E36.6"),sQuery(id+"F9.wireOp",EDGE,"E36.7"),sQuery(id+"F9.wireOp",EDGE,"E36.8"),sQuery(id+"F9.wireOp",EDGE,"E36.9")])]});
            var Q6;
            Q6=makeQuery(id+"F10.opExtrude","SWEPT_BODY",BODY,{"disambiguationData":[OSD([sQuery(id+"F9.wireOp",EDGE,"E35.0"),sQuery(id+"F9.wireOp",EDGE,"E35.1"),sQuery(id+"F9.wireOp",EDGE,"E35.2"),sQuery(id+"F9.wireOp",EDGE,"E35.3"),sQuery(id+"F9.wireOp",EDGE,"E35.4"),sQuery(id+"F9.wireOp",EDGE,"E35.5"),sQuery(id+"F9.wireOp",EDGE,"E35.6"),sQuery(id+"F9.wireOp",EDGE,"E35.7"),sQuery(id+"F9.wireOp",EDGE,"E35.8"),sQuery(id+"F9.wireOp",EDGE,"E35.9")])]});
            var Q7;
            Q7=makeQuery(id+"F10.opExtrude","SWEPT_BODY",BODY,{"disambiguationData":[OSD([sQuery(id+"F9.wireOp",EDGE,"E34.0"),sQuery(id+"F9.wireOp",EDGE,"E34.1"),sQuery(id+"F9.wireOp",EDGE,"E34.2"),sQuery(id+"F9.wireOp",EDGE,"E34.3"),sQuery(id+"F9.wireOp",EDGE,"E34.4"),sQuery(id+"F9.wireOp",EDGE,"E34.5"),sQuery(id+"F9.wireOp",EDGE,"E34.6"),sQuery(id+"F9.wireOp",EDGE,"E34.7"),sQuery(id+"F9.wireOp",EDGE,"E34.8"),sQuery(id+"F9.wireOp",EDGE,"E34.9")])]});
            var Q8;
            Q8=makeQuery(id+"F10.opExtrude","SWEPT_BODY",BODY,{"disambiguationData":[OSD([sQuery(id+"F9.wireOp",EDGE,"E33.0"),sQuery(id+"F9.wireOp",EDGE,"E33.1"),sQuery(id+"F9.wireOp",EDGE,"E33.2"),sQuery(id+"F9.wireOp",EDGE,"E33.3"),sQuery(id+"F9.wireOp",EDGE,"E33.4"),sQuery(id+"F9.wireOp",EDGE,"E33.5"),sQuery(id+"F9.wireOp",EDGE,"E33.6"),sQuery(id+"F9.wireOp",EDGE,"E33.7"),sQuery(id+"F9.wireOp",EDGE,"E33.8"),sQuery(id+"F9.wireOp",EDGE,"E33.9")])]});
            var Q9;
            Q9=sQuery(id+"F11.wireOp",EDGE,"E37");
            transform(context, id + "F12", {"entities" : qUnion([Q0, Q1, Q2, Q3, Q4, Q5, Q6, Q7, Q8]), "transformType" : TransformType.ROTATION, "transformAxis" : qUnion([Q9]), "angle" : 45 * degree, "makeCopy" : false});
        }
    });
